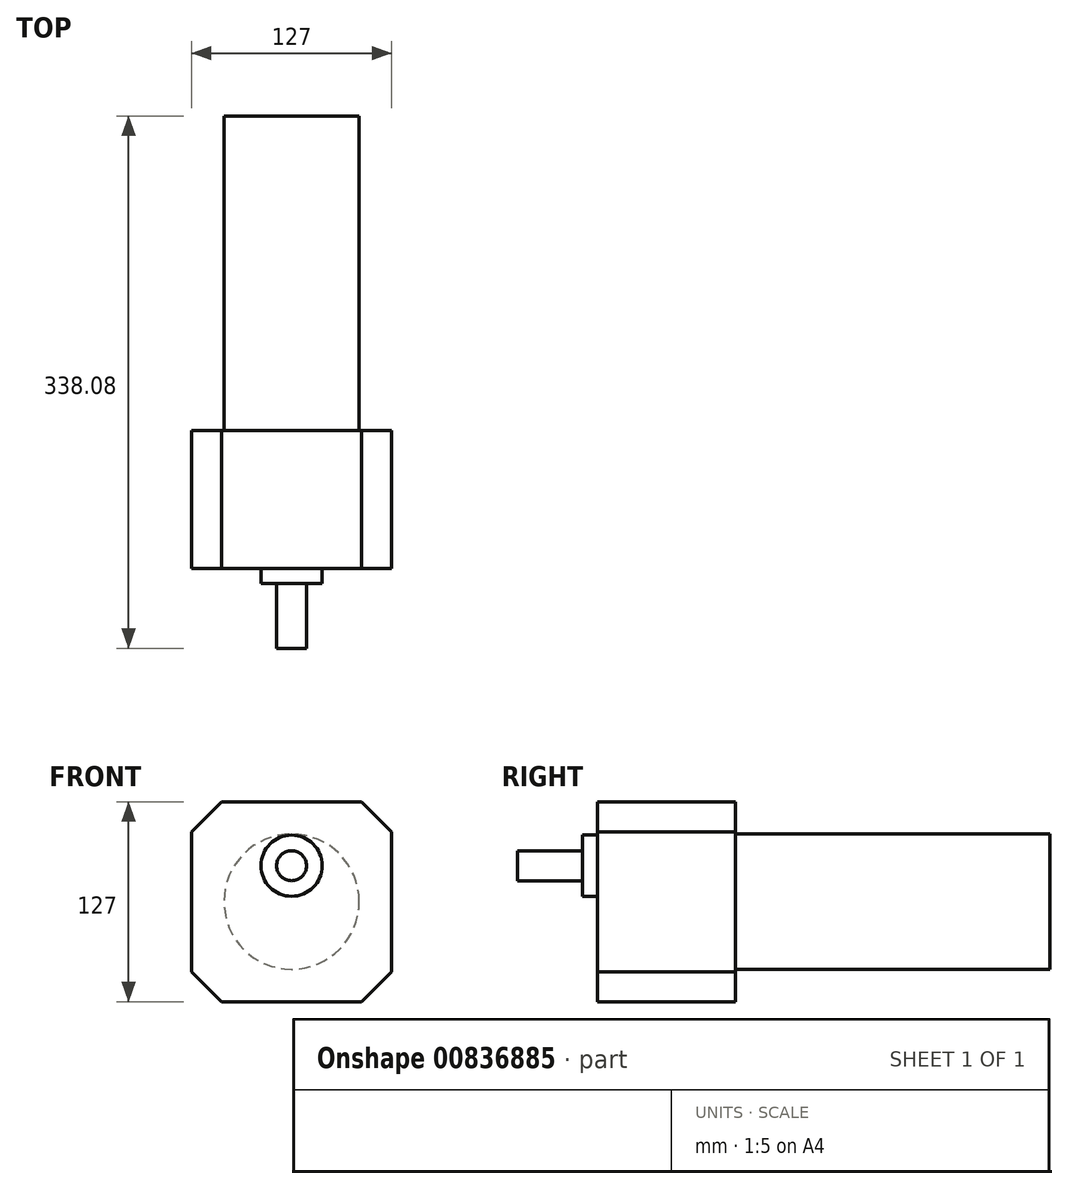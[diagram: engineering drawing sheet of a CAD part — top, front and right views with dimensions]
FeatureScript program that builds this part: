
annotation { "Feature Type Name" : "Feature", "Feature Type Description" : "" }
export const myFeature = defineFeature(function(context is Context, id is Id, definition is map)
    precondition{}
    {
        {
            var Q0;
            Q0=qCreatedBy(makeId("Front.planeOp"),FACE);
            var sketch = newSketch(context, id + "F0", { "sketchPlane" : qUnion([Q0])});
            skCircle(sketch, "E0", {"center": v(0, 0) * mm, "radius": 9.53 * mm});
            skSolve(sketch);
        }
        {
            var Q0;
            Q0 = qSketchRegion(id + "F0", true);
            extrude(context, id + "F1", {"entities" : qUnion([Q0]), "depth" : 41.27 * mm, "offsetDistance" : 25.4 * mm});
        }
        {
            var Q0;
            Q0=makeQuery(id+"F1.opExtrude","CAP_FACE",FACE,{"disambiguationData":[OSD([sQuery(id+"F0.wireOp",EDGE,"E0")])],"isStart":true});
            var sketch = newSketch(context, id + "F2", { "sketchPlane" : qUnion([Q0])});
            skCircle(sketch, "E1", {"center": v(0, 0) * mm, "radius": 19.43 * mm});
            skSolve(sketch);
        }
        {
            var Q0;
            Q0 = qSketchRegion(id + "F2", true);
            extrude(context, id + "F3", {"entities" : qUnion([Q0]), "operationType" : NewBodyOperationType.ADD, "depth" : 9.52 * mm, "offsetDistance" : 25.4 * mm});
        }
        {
            var Q0;
            Q0=makeQuery(id+"F3.opExtrude","CAP_FACE",FACE,{"disambiguationData":[OSD([sQuery(id+"F2.wireOp",EDGE,"E1")])],"isStart":false});
            var sketch = newSketch(context, id + "F4", { "sketchPlane" : qUnion([Q0])});
            skLineSegment(sketch, "E2.bottom", {"start": v(63.5, 40.64) * mm, "end": v(-63.5, 40.64) * mm});
            skLineSegment(sketch, "E2.top", {"start": v(63.5, -86.36) * mm, "end": v(-63.5, -86.36) * mm});
            skLineSegment(sketch, "E2.left", {"start": v(63.5, 40.64) * mm, "end": v(63.5, -86.36) * mm});
            skLineSegment(sketch, "E2.right", {"start": v(-63.5, 40.64) * mm, "end": v(-63.5, -86.36) * mm});
            skPoint(sketch, "E2.middle", {"position": v(0, -22.86) * mm});
            skSolve(sketch);
        }
        {
            var Q0;
            Q0 = qSketchRegion(id + "F4", true);
            extrude(context, id + "F5", {"entities" : qUnion([Q0]), "operationType" : NewBodyOperationType.ADD, "depth" : 87.63 * mm, "offsetDistance" : 25.4 * mm});
        }
        {
            var Q0;
            Q0=makeQuery(id+"F5.opExtrude","SWEPT_EDGE",EDGE,{"disambiguationData":[OSD([sQuery(id+"F4.wireOp",EDGE,"E2.bottom"),sQuery(id+"F4.wireOp",EDGE,"E2.right")])]});
            var Q1;
            Q1=makeQuery(id+"F5.opExtrude","SWEPT_EDGE",EDGE,{"disambiguationData":[OSD([sQuery(id+"F4.wireOp",EDGE,"E2.bottom"),sQuery(id+"F4.wireOp",EDGE,"E2.left")])]});
            var Q2;
            Q2=makeQuery(id+"F5.opExtrude","SWEPT_EDGE",EDGE,{"disambiguationData":[OSD([sQuery(id+"F4.wireOp",EDGE,"E2.top"),sQuery(id+"F4.wireOp",EDGE,"E2.right")])]});
            var Q3;
            Q3=makeQuery(id+"F5.opExtrude","SWEPT_EDGE",EDGE,{"disambiguationData":[OSD([sQuery(id+"F4.wireOp",EDGE,"E2.top"),sQuery(id+"F4.wireOp",EDGE,"E2.left")])]});
            chamfer(context, id + "F6", {"entities" : qUnion([Q0, Q1, Q2, Q3]), "width" : 19.05 * mm, "tangentPropagation" : true});
        }
        {
            var Q0;
            Q0=makeQuery(id+"F5.opExtrude","CAP_FACE",FACE,{"disambiguationData":[OSD([sQuery(id+"F4.wireOp",EDGE,"E2.bottom"),sQuery(id+"F4.wireOp",EDGE,"E2.top"),sQuery(id+"F4.wireOp",EDGE,"E2.left"),sQuery(id+"F4.wireOp",EDGE,"E2.right")])],"isStart":false});
            var sketch = newSketch(context, id + "F7", { "sketchPlane" : qUnion([Q0])});
            skCircle(sketch, "E3", {"center": v(0, -22.86) * mm, "radius": 42.93 * mm});
            skSolve(sketch);
        }
        {
            var Q0;
            Q0=makeQuery(id+"F7.imprint","IMPRINT",FACE,{"disambiguationData":[TD([[makeQuery(id+"F7.imprint","IMPRINT",EDGE,{"derivedFrom":sQuery(id+"F7.wireOp",EDGE,"E3")}),1.0]])]});
            extrude(context, id + "F8", {"entities" : qUnion([Q0]), "operationType" : NewBodyOperationType.ADD, "depth" : 199.64 * mm, "offsetDistance" : 25.4 * mm});
        }
    });
